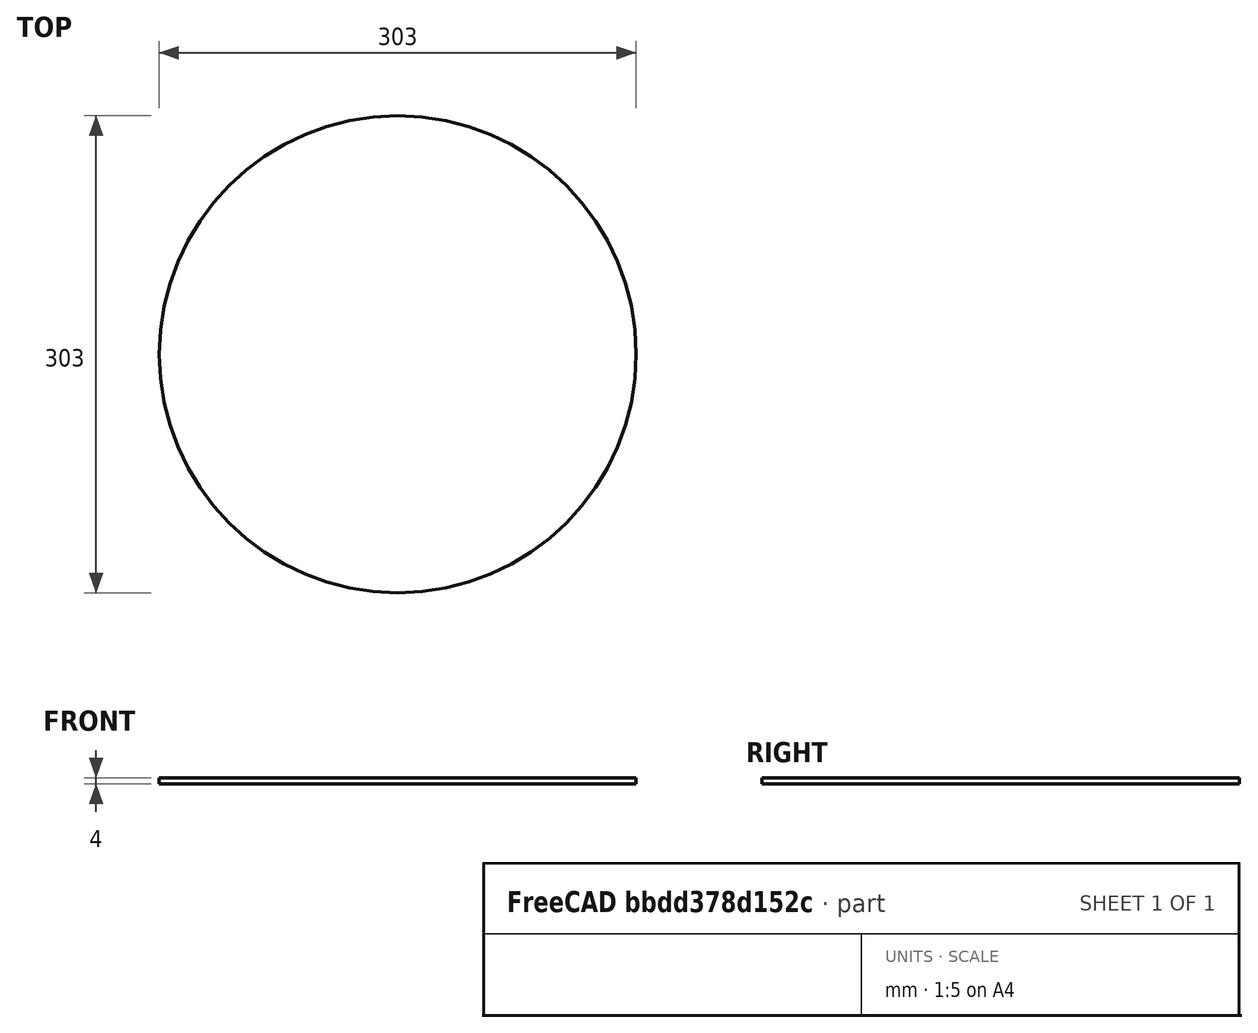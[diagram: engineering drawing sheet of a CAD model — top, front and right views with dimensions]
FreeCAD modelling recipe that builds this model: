
FCSTD DOCUMENT  (FreeCAD 1.1R20260106 (Git shallow))
Label: StopNU_glass
License: Creative Commons Attribution 4.0
LicenseURL: https://creativecommons.org/licenses/by/4.0/
objects: App::Point×1, Sketcher::SketchObject×1, PartDesign::Pad×1, PartDesign::Body×1
note: 6 computed .brp shape members not serialized (recipe doc carries the construction recipe); baked Part::Feature solids carry a one-line shape summary decoded from their .brp

FEATURE [App::Point] Origin001
  Role = Origin
FEATURE [Sketcher::SketchObject] Sketch
  ArcFitTolerance = 1e-06
  AttachmentSupport = -> [Origin]
  ExternalTypes = [0]
  FullyConstrained = true
  MakeInternals = false
  MapMode = 5
  sketch-geometry (1):
    g0: Circle CenterX=0 CenterY=0 CenterZ=0 NormalX=0 NormalY=0 NormalZ=1 AngleXU=0 Radius=151.5
  constraints (2):
    c: Diameter(g0) = 303
    c: Coincident(g0,g-1)
FEATURE [PartDesign::Pad] Pad
  Direction = (0,0,1)
  Length = 4
  Length2 = 10
  Profile = -> Sketch
  ReferenceAxis = -> Sketch [N_Axis]
  Refine = true
  SideType = 0
  Suppressed = false
  Type = 0
  Type2 = 0
FEATURE [PartDesign::Body] Body
  AllowCompound = false
  Group = -> [Sketch,Pad]
  Origin = -> Origin
  Tip = -> Pad
